# Revit family: CADS_Vent-Axia_Lo-CarbonSentinelKineticAdvance
name_source: partatom
category: Mechanical Equipment
revit_build: Autodesk Revit 2015 (Build: 20160512_1515(x64)
units: mm (PartAtom-declared; Revit-internal decimal feet)

## types (2) — shared parameters
Apparent Load = 690 VA
AssetType = Fixed
Category = Pr_60_60_36:Heat recovery distribution equipment
Color = White
Description = Lo-Carbon Sentinel Kinetic Advance
DurationUnit = year
ExpectedLife = 20
Features = Humidistat/Wi-Fi Controlled
IfcExportAs = IfcAirToAirHeatRecoveryType
IfcExportType = USERDEFINED
Manufacturer = Vent-Axia Limited
Material = ABS Plastic
ModelNumber = 405215
Name = MVHR Unit
NominalHeight = 760 mm  [stored 2.49344 ft]
NominalLength = 660 mm  [stored 2.16535 ft]
NominalWidth = 443 mm  [stored 1.45341 ft]
NumberOfPoles = 1
RatedCurrent = 3 A
RatedVoltage = 230 V
Shape = Square
Size = 443mm x 660mm x 760mm 
285mm x 550mm x 550mm
SpigotDiameter = 125 mm  [stored 0.410105 ft]
SpigotHeight = 65 mm  [stored 0.213255 ft]
Version = 1.0
WarrantyDurationLabor = 2
WarrantyDurationMotors = 5
WarrantyDurationParts = 2
WarrantyDurationUnit = year

## per-type parameters (varying)
| type | Model | ModelReference |
| Advance S | Lo-Carbon Sentinal Kinetic Advance S | Lo-Carbon Sentinal Kinetic Advance S |
| Advance SX | Lo-Carbon Sentinal Kinetic Advance SX | Lo-Carbon Sentinal Kinetic Advance SX |

note: [stored X ft] marks values corroborated as IEEE doubles in the binary element streams (Revit-internal decimal feet)

## geometry (parser evidence)
native form markers: Sweep x5
no freeform markers — native parametric forms only
